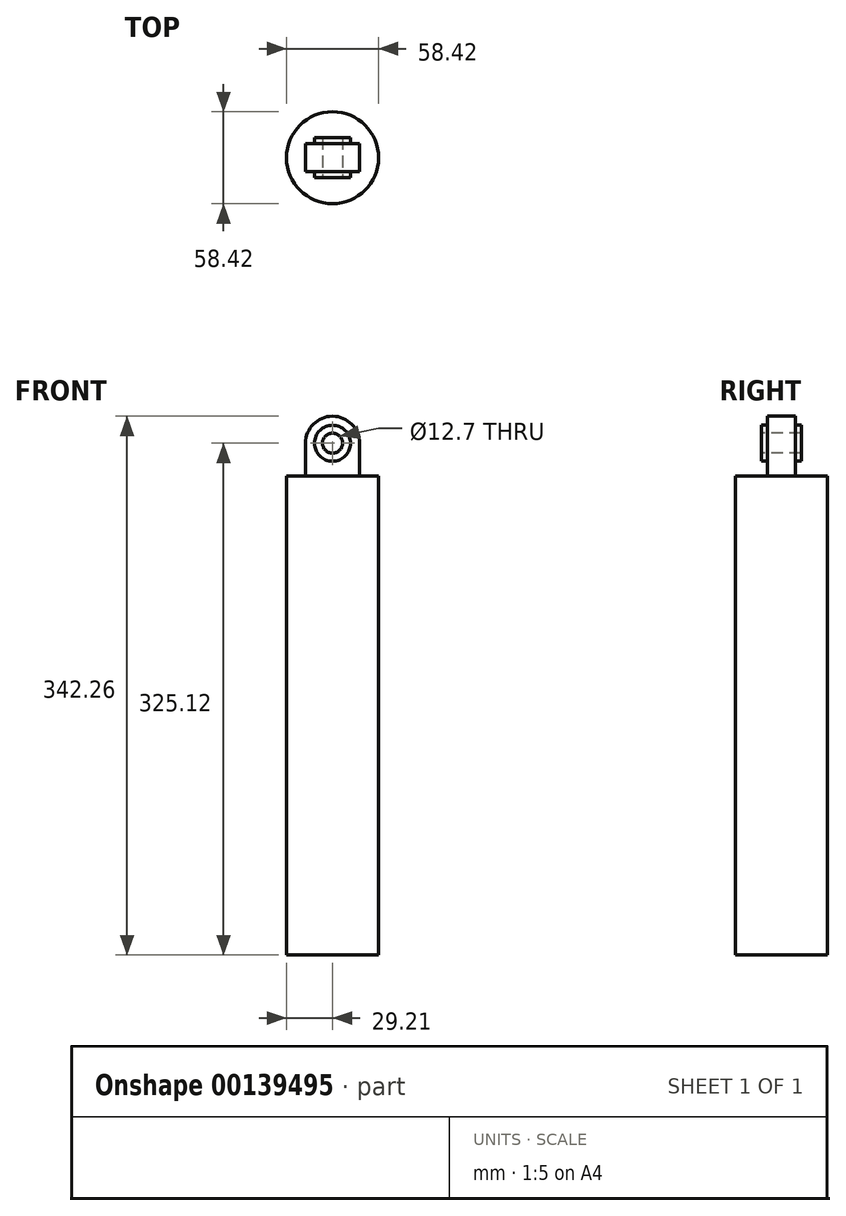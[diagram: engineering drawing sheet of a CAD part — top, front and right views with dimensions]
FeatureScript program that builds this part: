
annotation { "Feature Type Name" : "Feature", "Feature Type Description" : "" }
export const myFeature = defineFeature(function(context is Context, id is Id, definition is map)
    precondition{}
    {
        {
            var Q0;
            Q0=qCreatedBy(makeId("Top.planeOp"),FACE);
            var sketch = newSketch(context, id + "F0", { "sketchPlane" : qUnion([Q0])});
            skCircle(sketch, "E0", {"center": v(0, 0) * mm, "radius": 29.2 * mm});
            skSolve(sketch);
        }
        {
            var Q0;
            Q0=makeQuery(id+"F0.imprint","IMPRINT",FACE,{"disambiguationData":[TD([[makeQuery(id+"F0.imprint","IMPRINT",EDGE,{"derivedFrom":sQuery(id+"F0.wireOp",EDGE,"E0")}),1.0]])]});
            extrude(context, id + "F1", {"entities" : qUnion([Q0]), "depth" : 304.16 * mm});
        }
        {
            var Q0;
            Q0=makeQuery(id+"F1.opExtrude","CAP_FACE",FACE,{"disambiguationData":[OSD([sQuery(id+"F0.wireOp",EDGE,"E0")])],"isStart":false});
            var sketch = newSketch(context, id + "F2", { "sketchPlane" : qUnion([Q0])});
            skLineSegment(sketch, "E1.bottom", {"start": v(-17.14, -8.9) * mm, "end": v(17.15, -8.9) * mm});
            skLineSegment(sketch, "E1.top", {"start": v(-17.15, 8.9) * mm, "end": v(17.14, 8.9) * mm});
            skLineSegment(sketch, "E1.left", {"start": v(-17.14, -8.9) * mm, "end": v(-17.15, 8.9) * mm});
            skLineSegment(sketch, "E1.right", {"start": v(17.15, -8.9) * mm, "end": v(17.14, 8.9) * mm});
            skPoint(sketch, "E1.middle", {"position": v(0, 0) * mm});
            skSolve(sketch);
        }
        {
            var Q0;
            Q0=makeQuery(id+"F2.imprint","IMPRINT",FACE,{"disambiguationData":[TD([[makeQuery(id+"F2.imprint","IMPRINT",EDGE,{"derivedFrom":sQuery(id+"F2.wireOp",EDGE,"E1.bottom")}),1.0]])]});
            extrude(context, id + "F3", {"entities" : qUnion([Q0]), "operationType" : NewBodyOperationType.ADD, "depth" : 38.1 * mm});
        }
        {
            var Q0;
            Q0=makeQuery(id+"F3.opExtrude","CAP_EDGE",EDGE,{"disambiguationData":[OSD([sQuery(id+"F2.wireOp",EDGE,"E1.right")])],"isStart":false});
            var Q1;
            Q1=makeQuery(id+"F3.opExtrude","CAP_EDGE",EDGE,{"disambiguationData":[OSD([sQuery(id+"F2.wireOp",EDGE,"E1.left")])],"isStart":false});
            fillet(context, id + "F4", {"entities" : qUnion([Q0, Q1]), "radius" : 17.14 * mm, "tangentPropagation" : true, "allowEdgeOverflow" : false});
        }
        {
            var Q0;
            Q0=makeQuery(id+"F3.opExtrude","SWEPT_FACE",FACE,{"disambiguationData":[OSD([sQuery(id+"F2.wireOp",EDGE,"E1.top")])]});
            var sketch = newSketch(context, id + "F5", { "sketchPlane" : qUnion([Q0])});
            skCircle(sketch, "E2", {"center": v(0, 325.12) * mm, "radius": 11.43 * mm});
            skSolve(sketch);
        }
        {
            var Q0;
            Q0 = qSketchRegion(id + "F5", true);
            extrude(context, id + "F6", {"entities" : qUnion([Q0]), "operationType" : NewBodyOperationType.ADD, "depth" : 3.8 * mm});
        }
        {
            var Q0;
            Q0=makeQuery(id+"F3.opExtrude","SWEPT_FACE",FACE,{"disambiguationData":[OSD([sQuery(id+"F2.wireOp",EDGE,"E1.bottom")])]});
            var sketch = newSketch(context, id + "F7", { "sketchPlane" : qUnion([Q0])});
            skCircle(sketch, "E3", {"center": v(0, 325.12) * mm, "radius": 11.43 * mm});
            skSolve(sketch);
        }
        {
            var Q0;
            Q0=makeQuery(id+"F7.imprint","IMPRINT",FACE,{"disambiguationData":[TD([[makeQuery(id+"F7.imprint","IMPRINT",EDGE,{"derivedFrom":sQuery(id+"F7.wireOp",EDGE,"E3")}),1.0]])]});
            extrude(context, id + "F8", {"entities" : qUnion([Q0]), "operationType" : NewBodyOperationType.ADD, "depth" : 3.8 * mm});
        }
        {
            var Q0;
            Q0=makeQuery(id+"F8.opExtrude","CAP_FACE",FACE,{"disambiguationData":[OSD([sQuery(id+"F7.wireOp",EDGE,"E3")])],"isStart":false});
            var sketch = newSketch(context, id + "F9", { "sketchPlane" : qUnion([Q0])});
            skCircle(sketch, "E4", {"center": v(0, 325.12) * mm, "radius": 6.35 * mm});
            skSolve(sketch);
        }
        {
            var Q0;
            Q0 = qSketchRegion(id + "F9", true);
            extrude(context, id + "F10", {"entities" : qUnion([Q0]), "operationType" : NewBodyOperationType.REMOVE, "oppositeDirection" : true, "depth" : 38.1 * mm});
        }
    });
